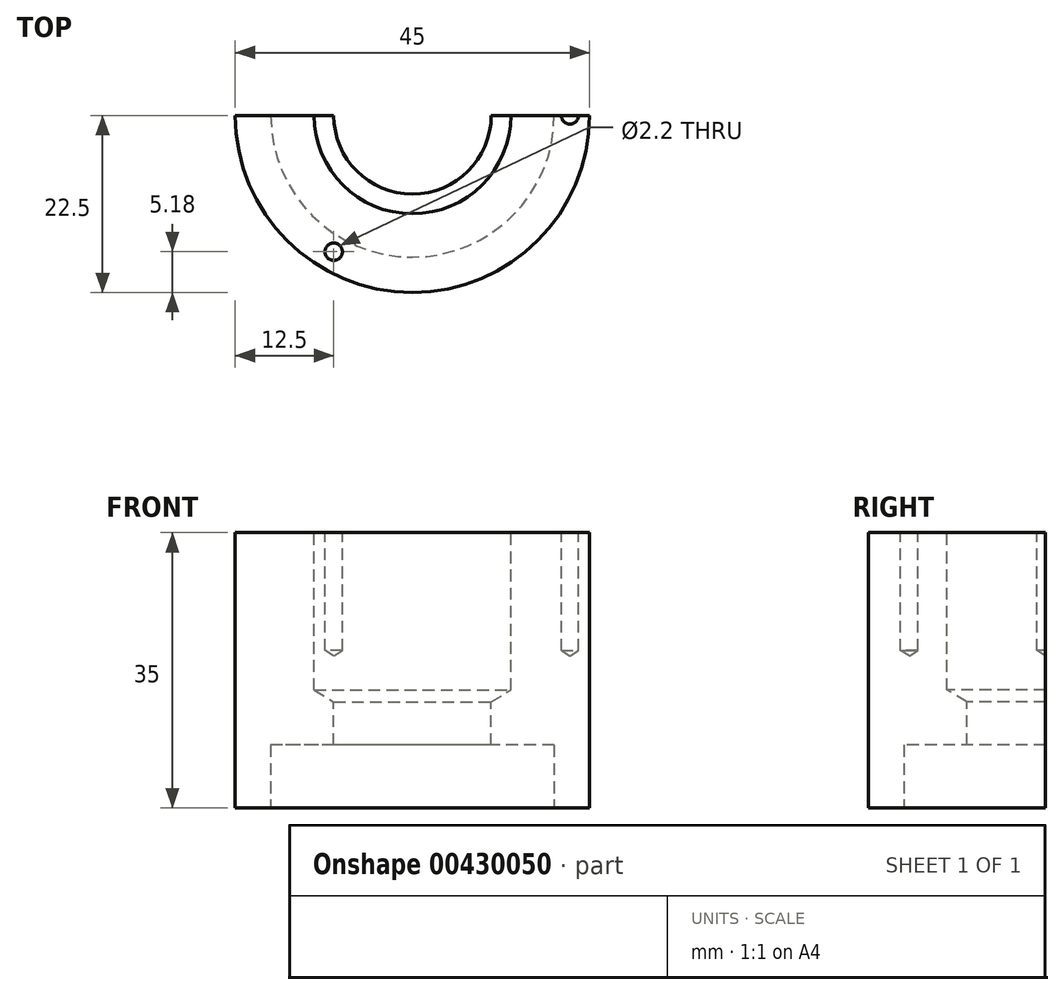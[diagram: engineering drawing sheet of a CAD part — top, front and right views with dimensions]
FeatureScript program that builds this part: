
annotation { "Feature Type Name" : "Feature", "Feature Type Description" : "" }
export const myFeature = defineFeature(function(context is Context, id is Id, definition is map)
    precondition{}
    {
        {
            var Q0;
            Q0=qCreatedBy(makeId("Top.planeOp"),FACE);
            var sketch = newSketch(context, id + "F0", { "sketchPlane" : qUnion([Q0])});
            skCircle(sketch, "E0", {"center": v(0, 0) * mm, "radius": 22.5 * mm});
            skSolve(sketch);
        }
        {
            var Q0;
            Q0=makeQuery(id+"F0.imprint","IMPRINT",FACE,{"disambiguationData":[TD([[makeQuery(id+"F0.imprint","IMPRINT",EDGE,{"derivedFrom":sQuery(id+"F0.wireOp",EDGE,"E0")}),1.0]])]});
            extrude(context, id + "F1", {"entities" : qUnion([Q0]), "depth" : 35 * mm});
        }
        {
            var Q0;
            Q0=makeQuery(id+"F1.opExtrude","CAP_FACE",FACE,{"disambiguationData":[OSD([sQuery(id+"F0.wireOp",EDGE,"E0")])],"isStart":true});
            var sketch = newSketch(context, id + "F2", { "sketchPlane" : qUnion([Q0])});
            skCircle(sketch, "E1", {"center": v(0, 0) * mm, "radius": 18 * mm});
            skSolve(sketch);
        }
        {
            var Q0;
            Q0=makeQuery(id+"F2.imprint","IMPRINT",FACE,{"disambiguationData":[TD([[makeQuery(id+"F2.imprint","IMPRINT",EDGE,{"derivedFrom":sQuery(id+"F2.wireOp",EDGE,"E1")}),1.0]])]});
            extrude(context, id + "F3", {"entities" : qUnion([Q0]), "operationType" : NewBodyOperationType.REMOVE, "oppositeDirection" : true, "depth" : 8 * mm});
        }
        {
            var Q0;
            Q0=makeQuery(id+"F1.opExtrude","CAP_FACE",FACE,{"disambiguationData":[OSD([sQuery(id+"F0.wireOp",EDGE,"E0")])],"isStart":false});
            var sketch = newSketch(context, id + "F4", { "sketchPlane" : qUnion([Q0])});
            skPoint(sketch, "E2", {"position": v(0, 0) * mm});
            skSolve(sketch);
        }
        {
            var Q0;
            Q0=sQuery(id+"F4.wireOp",VERTEX,"E2");
            var Q1;
            Q1=makeQuery(id+"F1.opExtrude","SWEPT_BODY",BODY,{"disambiguationData":[OSD([sQuery(id+"F0.wireOp",EDGE,"E0")])]});
            hole(context, id + "F5", {"style" : HoleStyle.SIMPLE, "endStyle" : HoleEndStyle.BLIND, "holeDiameter" : 25 * mm, "holeDepth" : 20 * mm, "isTappedThrough" : true, "tappedDepth" : 12 * mm, "tapClearance" : 3, "startFromSketch" : true, "locations" : qUnion([Q0]), "scope" : qUnion([Q1])});
        }
        {
            var Q0;
            Q0=sQuery(id+"F4.wireOp",VERTEX,"E2");
            var Q1;
            Q1=makeQuery(id+"F1.opExtrude","SWEPT_BODY",BODY,{"disambiguationData":[OSD([sQuery(id+"F0.wireOp",EDGE,"E0")])]});
            hole(context, id + "F6", {"style" : HoleStyle.SIMPLE, "endStyle" : HoleEndStyle.THROUGH, "holeDiameter" : 20 * mm, "isTappedThrough" : true, "tappedDepth" : 12 * mm, "tapClearance" : 3, "startFromSketch" : true, "locations" : qUnion([Q0]), "scope" : qUnion([Q1])});
        }
        {
            var Q0;
            Q0=makeQuery(id+"F4.imprint","IMPRINT",FACE,{"disambiguationData":[TD([[makeQuery(id+"F4.imprint","IMPRINT",EDGE,{"derivedFrom":makeQuery(id+"F1.opExtrude","CAP_EDGE",EDGE,{"disambiguationData":[OSD([sQuery(id+"F0.wireOp",EDGE,"E0")])],"isStart":false})}),1.0]])]});
            var sketch = newSketch(context, id + "F7", { "sketchPlane" : qUnion([Q0])});
            skPoint(sketch, "E3", {"position": v(20, 0) * mm});
            skPoint(sketch, "E4.1.0", {"position": v(-10, -17.32) * mm});
            skPoint(sketch, "E4.2.0", {"position": v(-10, 17.32) * mm});
            skPoint(sketch, "E4.center", {"position": v(0, 0) * mm});
            skLineSegment(sketch, "E4.anchor1", {"start": v(0, 0) * mm, "end": v(20, 0) * mm, "construction": true});
            skLineSegment(sketch, "E4.anchor2", {"start": v(0, 0) * mm, "end": v(-10, 17.32) * mm, "construction": true});
            skSolve(sketch);
        }
        {
            var Q0;
            Q0=sQuery(id+"F7.wireOp",VERTEX,"E3");
            var Q1;
            Q1=sQuery(id+"F7.wireOp",VERTEX,"E4.2.0");
            var Q2;
            Q2=sQuery(id+"F7.wireOp",VERTEX,"E4.1.0");
            var Q3;
            Q3=makeQuery(id+"F1.opExtrude","SWEPT_BODY",BODY,{"disambiguationData":[OSD([sQuery(id+"F0.wireOp",EDGE,"E0")])]});
            hole(context, id + "F8", {"style" : HoleStyle.SIMPLE, "endStyle" : HoleEndStyle.BLIND, "holeDiameter" : 2.2 * mm, "holeDepth" : 15 * mm, "isTappedThrough" : true, "tappedDepth" : 12 * mm, "tapClearance" : 3, "startFromSketch" : true, "locations" : qUnion([Q0, Q1, Q2]), "scope" : qUnion([Q3])});
        }
        {
            var Q0;
            Q0=qCreatedBy(makeId("Front.planeOp"),FACE);
            var sketch = newSketch(context, id + "F9", { "sketchPlane" : qUnion([Q0])});
            skLineSegment(sketch, "E5.bottom", {"start": v(29.3, -5.62) * mm, "end": v(-30.7, -5.62) * mm});
            skLineSegment(sketch, "E5.top", {"start": v(29.3, 45.33) * mm, "end": v(-30.7, 45.33) * mm});
            skLineSegment(sketch, "E5.left", {"start": v(29.3, -5.62) * mm, "end": v(29.3, 45.33) * mm});
            skLineSegment(sketch, "E5.right", {"start": v(-30.7, -5.62) * mm, "end": v(-30.7, 45.33) * mm});
            skSolve(sketch);
        }
        {
            var Q0;
            Q0=makeQuery(id+"F9.imprint","IMPRINT",FACE,{"disambiguationData":[TD([[makeQuery(id+"F9.imprint","IMPRINT",EDGE,{"derivedFrom":sQuery(id+"F9.wireOp",EDGE,"E5.bottom")}),-1.0]])]});
            extrude(context, id + "F10", {"entities" : qUnion([Q0]), "operationType" : NewBodyOperationType.REMOVE, "oppositeDirection" : true, "depth" : 25 * mm});
        }
    });
